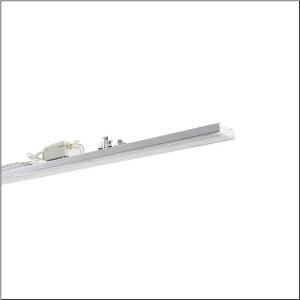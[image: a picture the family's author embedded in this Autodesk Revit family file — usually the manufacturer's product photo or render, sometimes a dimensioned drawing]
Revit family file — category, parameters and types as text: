
# Revit family: licross_r__21_recessed_ho_52tl12dv4l2m3s_7bf3
name_source: partatom
category: Lighting Fixtures
units: mm (PartAtom-declared; Revit-internal decimal feet)

## family parameters
Cut with Voids When Loaded = No
Host = Face
Light Source = No
Part Type = Normal
Room Calculation Point = No
Round Connector Dimension = Use Diameter
Shared = No

## types (1)
- --- (1 x LED, 910 lm, 6.4 W, 4000K)
    Apparent Load = 6 VA
    CIE Flux Codes = 69 91 98 100 100
    Color Rendering = 80
    Color Temperature = 4000K
    Default Elevation = 1800 mm
    Description = Licross® 21 Recessed HO, luminaire insert, of sheet steel, galvanised, coil coated, white, length: 2.250mm, width: 66mm, height: 67mm, LED rated luminous flux: 22.710lm, light colour: 840, control gear: DALI 2, with plug, 6-pole, with phase selection, for trunking rail, 14-core, mains connection: 220..240V, AC, 50/60Hz, rated input power: 129W, for trunking rail, 14-core, halogen-free wiring, for emergency light function, converter,control gear: single battery element, battery: LiFeP04, 9Ah, primary optical cover: cover, of PMMA, light emission: direct distribution, primary light characteristic: symmetric, protection rating (complete): IP40, insulation class (complete): insulation class I (protective earthing), certification: CE, UKCA, protection symbol: D if used in an environment without relevant dust loads with corresponding accessories, impact resistance: IK06, permissible ambient temperature for indoor applications: +5..+30°C, standard: EN 60598-2-22, LABS conformity tested according to VDMA 24364:2018-05, reducing of maximum allowable ambient temperature of 5°C with ceiling mounting, corresponds to IFS (International Featured Standards) requirements for safety and quality in the food industry, packaging unit: 1 piece
    Height = 58 mm
    Lamp = 1 x LED
    Lamp Light Flux = 910 lm
    Lamp Power = 6.4 W
    Lamp count = 1
    Length = 2250 mm
    Luminous efficacy = 142 lm/W
    Manufacturer = Siteco
    ModVariant = No
    Model = 52TL12DV4L2M3S
    Mounting Place = Ceiling
    Mounting Type = Pendant
    Number of Poles = 1
    OnlyDefault = Yes
    Power Factor = 1
    Product Name = Licross® 21 Recessed HO
    Product group = luminaire insert
    ProductGroupID = 901
    Protection Class = Protection class I
    Protection Degree = IP 40
    RLX_Detail_Level = 1
    RLX_Emergency_Light_Flux = 0 lm
    RLX_Emergency_Type = 0
    RLX_Emergency_Type_DB = No
    RlxData = <blob elided: 30125 chars, md5=d9acbdc7>
    Socket = socket
    Standby Power = 0 W
    System Light Flux = 910 lm
    System Power = 6 W
    Type Comments = : emergency light operation: 3 h
    Type Image = l_1296930.jpg
    URL = http://relux.com
    VarID = @adj_039463
    Voltage = 0 V
    Weight = 0.00 kg
    Width = 66 mm

## geometry (parser evidence)
native form markers: Blend x4, Sweep x11
no freeform markers — native parametric forms only
